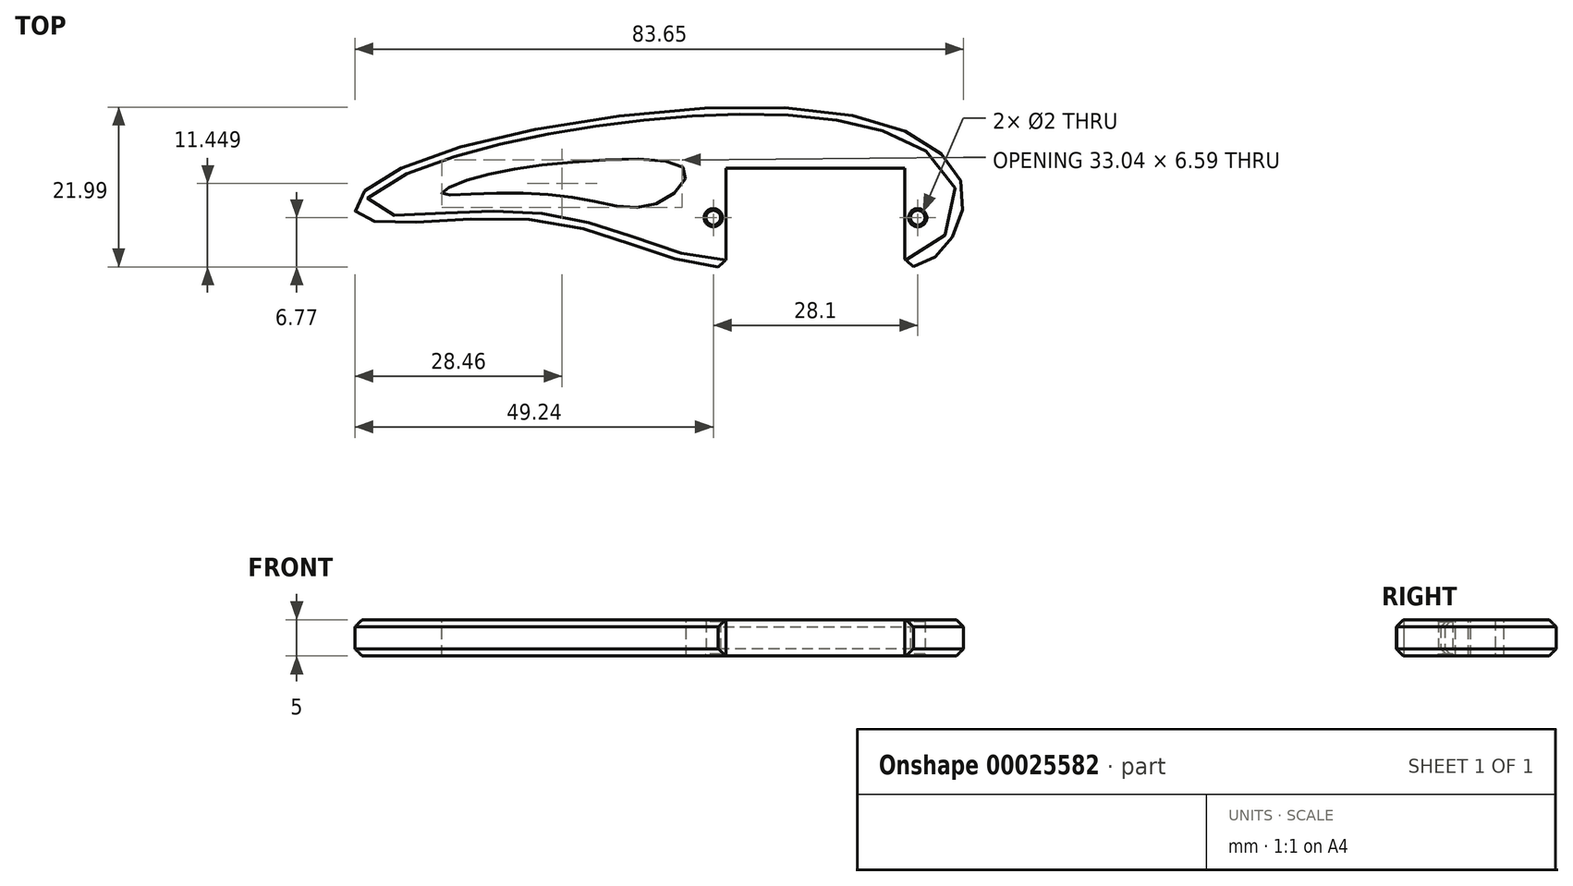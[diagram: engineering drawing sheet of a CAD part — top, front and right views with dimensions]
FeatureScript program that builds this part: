
annotation { "Feature Type Name" : "Feature", "Feature Type Description" : "" }
export const myFeature = defineFeature(function(context is Context, id is Id, definition is map)
    precondition{}
    {
        {
            var Q0;
            Q0=qCreatedBy(makeId("Top.planeOp"),FACE);
            var sketch = newSketch(context, id + "F0", { "sketchPlane" : qUnion([Q0])});
            skLineSegment(sketch, "E0.bottom", {"start": v(0, 0) * mm, "end": v(24.6, 0) * mm});
            skLineSegment(sketch, "E0.top", {"start": v(0, 13.6) * mm, "end": v(24.6, 13.6) * mm});
            skLineSegment(sketch, "E0.left", {"start": v(0, 0) * mm, "end": v(0, 13.6) * mm});
            skLineSegment(sketch, "E0.right", {"start": v(24.6, 0) * mm, "end": v(24.6, 13.6) * mm});
            skFitSpline(sketch, "E1", {"points": [v(24.6, 0) * mm, v(30.36, 3) * mm, v(32.32, 11.67) * mm, v(12.1, 21.62) * mm, v(-48.13, 11.71) * mm, v(-50.4, 6.95) * mm, v(-25, 6.36) * mm, v(0, 0) * mm], "startDerivative": vector(88.58, 0) * mm, "endDerivative": vector(145.14, 0) * mm});
            skPoint(sketch, "E2", {"position": v(19.6, 6.8) * mm});
            skLineSegment(sketch, "E3", {"start": v(0, 6.8) * mm, "end": v(-1.75, 6.8) * mm, "construction": true});
            skLineSegment(sketch, "E4", {"start": v(24.6, 6.8) * mm, "end": v(26.35, 6.8) * mm, "construction": true});
            skCircle(sketch, "E5", {"center": v(-1.75, 6.8) * mm, "radius": 1 * mm});
            skCircle(sketch, "E6", {"center": v(26.35, 6.8) * mm, "radius": 1 * mm});
            skSolve(sketch);
        }
        {
            var Q0;
            Q0=makeQuery(id+"F0.imprint","IMPRINT",FACE,{"disambiguationData":[TD([[makeQuery(id+"F0.imprint","IMPRINT",EDGE,{"derivedFrom":sQuery(id+"F0.wireOp",EDGE,"E0.top")}),1.0]])]});
            extrude(context, id + "F1", {"entities" : qUnion([Q0]), "depth" : 5 * mm});
        }
        {
            var Q0;
            Q0=makeQuery(id+"F1.opExtrude","CAP_FACE",FACE,{"disambiguationData":[OSD([sQuery(id+"F0.wireOp",EDGE,"E0.top"),sQuery(id+"F0.wireOp",EDGE,"E0.left"),sQuery(id+"F0.wireOp",EDGE,"E0.right"),sQuery(id+"F0.wireOp",EDGE,"E1"),sQuery(id+"F0.wireOp",EDGE,"E5"),sQuery(id+"F0.wireOp",EDGE,"E6")])],"isStart":false});
            var sketch = newSketch(context, id + "F2", { "sketchPlane" : qUnion([Q0])});
            skFitSpline(sketch, "E7", {"points": [v(-31.47, 10.2) * mm, v(-18.51, 9.12) * mm, v(-9.46, 8.73) * mm, v(-5.55, 13.22) * mm, v(-19.22, 14.57) * mm, v(-35.2, 12.07) * mm, v(-39.07, 10.12) * mm, v(-31.47, 10.2) * mm]});
            skSolve(sketch);
        }
        {
            var Q0;
            Q0=makeQuery(id+"F2.imprint","IMPRINT",FACE,{"disambiguationData":[TD([[makeQuery(id+"F2.imprint","IMPRINT",EDGE,{"derivedFrom":sQuery(id+"F2.wireOp",EDGE,"E7")}),1.0]])]});
            extrude(context, id + "F3", {"entities" : qUnion([Q0]), "operationType" : NewBodyOperationType.REMOVE, "endBound" : BoundingType.UP_TO_NEXT, "oppositeDirection" : true, "depth" : 25 * mm});
        }
        {
            var Q0;
            Q0=makeQuery(id+"F1.opExtrude","CAP_EDGE",EDGE,{"disambiguationData":[OSD([sQuery(id+"F0.wireOp",EDGE,"E1")])],"isStart":false});
            var Q1;
            Q1=makeQuery(id+"F1.opExtrude","CAP_EDGE",EDGE,{"disambiguationData":[OSD([sQuery(id+"F0.wireOp",EDGE,"E1")])],"isStart":true});
            var Q2;
            Q2=makeQuery(id+"F3.boolean.opBoolean","COPY",EDGE,{"derivedFrom":makeQuery(id+"F3.opExtrude","CAP_EDGE",EDGE,{"disambiguationData":[OSD([sQuery(id+"F2.wireOp",EDGE,"E7")])],"isStart":true})});
            var Q3;
            Q3=makeQuery(id+"F3.boolean.opBoolean","COPY",EDGE,{"derivedFrom":makeQuery(id+"F3.opExtrude","TWEAK_EDGE",EDGE,{"derivedFrom":[makeQuery(id+"F1.opExtrude","CAP_FACE",FACE,{"disambiguationData":[OSD([sQuery(id+"F0.wireOp",EDGE,"E0.top"),sQuery(id+"F0.wireOp",EDGE,"E0.left"),sQuery(id+"F0.wireOp",EDGE,"E0.right"),sQuery(id+"F0.wireOp",EDGE,"E1"),sQuery(id+"F0.wireOp",EDGE,"E5"),sQuery(id+"F0.wireOp",EDGE,"E6")])],"isStart":true}),makeQuery(id+"F2.imprint","IMPRINT",EDGE,{"derivedFrom":sQuery(id+"F2.wireOp",EDGE,"E7")})]})});
            var Q4;
            Q4=makeQuery(id+"F1.opExtrude","SWEPT_EDGE",EDGE,{"disambiguationData":[OSD([sQuery(id+"F0.wireOp",EDGE,"E0.bottom"),sQuery(id+"F0.wireOp",EDGE,"E0.left"),sQuery(id+"F0.wireOp",EDGE,"E1")])]});
            var Q5;
            Q5=makeQuery(id+"F1.opExtrude","SWEPT_EDGE",EDGE,{"disambiguationData":[OSD([sQuery(id+"F0.wireOp",EDGE,"E0.bottom"),sQuery(id+"F0.wireOp",EDGE,"E0.right"),sQuery(id+"F0.wireOp",EDGE,"E1")])]});
            chamfer(context, id + "F4", {"entities" : qUnion([Q0, Q1, Q2, Q3, Q4, Q5]), "width" : 1 * mm, "tangentPropagation" : true});
        }
        {
            var Q0;
            Q0=makeQuery(id+"F1.opExtrude","CAP_EDGE",EDGE,{"disambiguationData":[OSD([sQuery(id+"F0.wireOp",EDGE,"E5")])],"isStart":false});
            var Q1;
            Q1=makeQuery(id+"F1.opExtrude","CAP_EDGE",EDGE,{"disambiguationData":[OSD([sQuery(id+"F0.wireOp",EDGE,"E6")])],"isStart":false});
            var Q2;
            Q2=makeQuery(id+"F1.opExtrude","CAP_EDGE",EDGE,{"disambiguationData":[OSD([sQuery(id+"F0.wireOp",EDGE,"E5")])],"isStart":true});
            var Q3;
            Q3=makeQuery(id+"F1.opExtrude","CAP_EDGE",EDGE,{"disambiguationData":[OSD([sQuery(id+"F0.wireOp",EDGE,"E6")])],"isStart":true});
            chamfer(context, id + "F5", {"entities" : qUnion([Q0, Q1, Q2, Q3]), "width" : 0.25 * mm, "tangentPropagation" : true});
        }
    });
